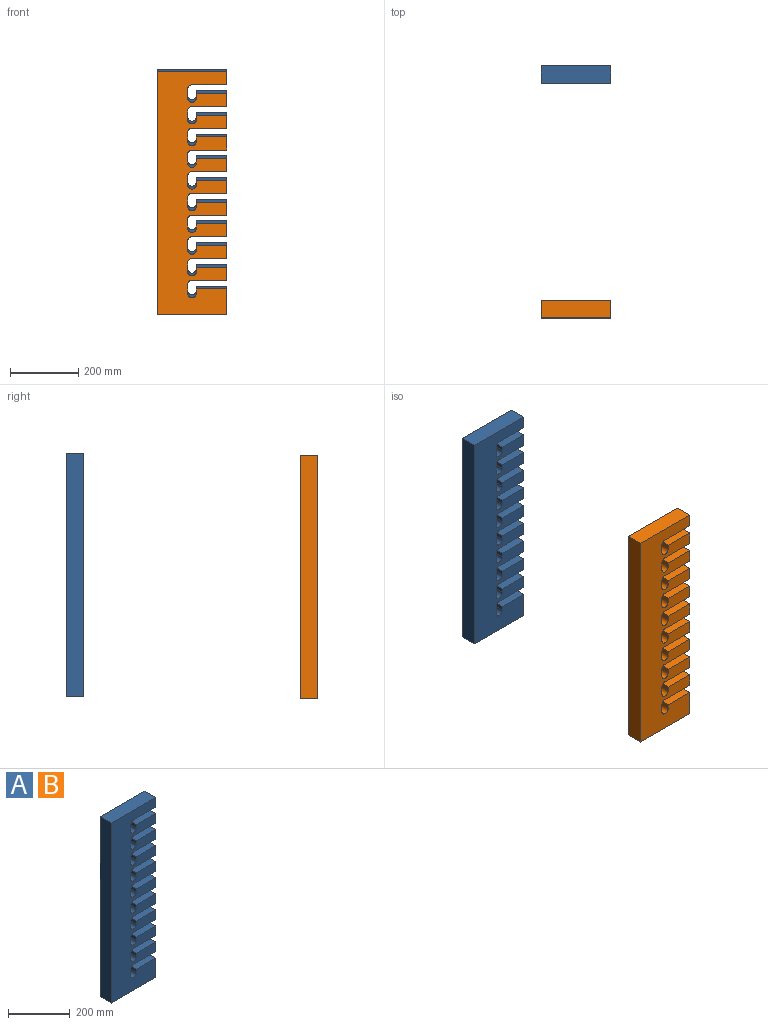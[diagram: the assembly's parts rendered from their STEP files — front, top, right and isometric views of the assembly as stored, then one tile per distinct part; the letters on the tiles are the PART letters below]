
ASSEMBLY  parts=2 mates=2
PART A: 76 faces, bbox 203.2x50.8x711.2 mm
  f0: plane 88.9x50.8mm, normal (0,0,1), area 4516.1mm2, adj f1,f73,f74,f75
  f1: plane 50.8x12.7mm, normal (-1,0,0), area 645.2mm2, adj f0,f2,f74,f75
  f2: cylinder r=12.7mm len=50.8mm, axis (0,1,0), area 2026.8mm2, adj f1,f3,f74,f75
  f3: plane 50.8x25.4mm, normal (1,0,0), area 1290.3mm2, adj f2,f4,f74,f75
  f4: cylinder r=12.7mm len=50.8mm, axis (0,1,0), area 1013.4mm2, adj f3,f5,f74,f75
  f5: plane 101.6x50.8mm, normal (0,0,-1), area 5161.3mm2, adj f4,f6,f74,f75
  f6: plane 50.8x38.1mm, normal (1,0,0), area 1935.5mm2, adj f5,f7,f74,f75
  f7: plane 88.9x50.8mm, normal (0,0,1), area 4516.1mm2, adj f6,f8,f74,f75
  f8: plane 50.8x12.7mm, normal (-1,0,0), area 645.2mm2, adj f7,f9,f74,f75
  f9: cylinder r=12.7mm len=50.8mm, axis (0,1,0), area 2026.8mm2, adj f8,f10,f74,f75
  f10: plane 50.8x25.4mm, normal (1,0,0), area 1290.3mm2, adj f9,f11,f74,f75
  f11: cylinder r=12.7mm len=50.8mm, axis (0,1,0), area 1013.4mm2, adj f10,f12,f74,f75
  f12: plane 101.6x50.8mm, normal (0,0,-1), area 5161.3mm2, adj f11,f13,f74,f75
  f13: plane 50.8x38.1mm, normal (1,0,0), area 1935.5mm2, adj f12,f14,f74,f75
  f14: plane 88.9x50.8mm, normal (0,0,1), area 4516.1mm2, adj f13,f15,f74,f75
  f15: plane 50.8x12.7mm, normal (-1,0,0), area 645.2mm2, adj f14,f16,f74,f75
  f16: cylinder r=12.7mm len=50.8mm, axis (0,1,0), area 2026.8mm2, adj f15,f17,f74,f75
  f17: plane 50.8x25.4mm, normal (1,0,0), area 1290.3mm2, adj f16,f18,f74,f75
  f18: cylinder r=12.7mm len=50.8mm, axis (0,1,0), area 1013.4mm2, adj f17,f19,f74,f75
  f19: plane 101.6x50.8mm, normal (0,0,-1), area 5161.3mm2, adj f18,f20,f74,f75
  f20: plane 50.8x38.1mm, normal (1,0,0), area 1935.5mm2, adj f19,f21,f74,f75
  f21: plane 88.9x50.8mm, normal (0,0,1), area 4516.1mm2, adj f20,f22,f74,f75
  f22: plane 50.8x12.7mm, normal (-1,0,0), area 645.2mm2, adj f21,f23,f74,f75
  f23: cylinder r=12.7mm len=50.8mm, axis (0,1,0), area 2026.8mm2, adj f22,f24,f74,f75
  f24: plane 50.8x25.4mm, normal (1,0,0), area 1290.3mm2, adj f23,f25,f74,f75
  f25: cylinder r=12.7mm len=50.8mm, axis (0,1,0), area 1013.4mm2, adj f24,f26,f74,f75
  f26: plane 101.6x50.8mm, normal (0,0,-1), area 5161.3mm2, adj f25,f27,f74,f75
  f27: plane 50.8x38.1mm, normal (1,0,0), area 1935.5mm2, adj f26,f28,f74,f75
  f28: plane 88.9x50.8mm, normal (0,0,1), area 4516.1mm2, adj f27,f29,f74,f75
  f29: plane 50.8x12.7mm, normal (-1,0,0), area 645.2mm2, adj f28,f30,f74,f75
  f30: cylinder r=12.7mm len=50.8mm, axis (0,1,0), area 2026.8mm2, adj f29,f31,f74,f75
  f31: plane 50.8x25.4mm, normal (1,0,0), area 1290.3mm2, adj f30,f32,f74,f75
  f32: cylinder r=12.7mm len=50.8mm, axis (0,1,0), area 1013.4mm2, adj f31,f33,f74,f75
  f33: plane 101.6x50.8mm, normal (0,0,-1), area 5161.3mm2, adj f32,f34,f74,f75
  f34: plane 50.8x38.1mm, normal (1,0,0), area 1935.5mm2, adj f33,f35,f74,f75
  f35: plane 88.9x50.8mm, normal (0,0,1), area 4516.1mm2, adj f34,f36,f74,f75
  f36: plane 50.8x12.7mm, normal (-1,0,0), area 645.2mm2, adj f35,f37,f74,f75
  f37: cylinder r=12.7mm len=50.8mm, axis (0,1,0), area 2026.8mm2, adj f36,f38,f74,f75
  f38: plane 50.8x25.4mm, normal (1,0,0), area 1290.3mm2, adj f37,f39,f74,f75
  f39: cylinder r=12.7mm len=50.8mm, axis (0,1,0), area 1013.4mm2, adj f38,f40,f74,f75
  f40: plane 101.6x50.8mm, normal (0,0,-1), area 5161.3mm2, adj f39,f41,f74,f75
  f41: plane 50.8x38.1mm, normal (1,0,0), area 1935.5mm2, adj f40,f42,f74,f75
  f42: plane 88.9x50.8mm, normal (0,0,1), area 4516.1mm2, adj f41,f43,f74,f75
  f43: plane 50.8x12.7mm, normal (-1,0,0), area 645.2mm2, adj f42,f44,f74,f75
  f44: cylinder r=12.7mm len=50.8mm, axis (0,1,0), area 2026.8mm2, adj f43,f45,f74,f75
  f45: plane 50.8x25.4mm, normal (1,0,0), area 1290.3mm2, adj f44,f46,f74,f75
  f46: cylinder r=12.7mm len=50.8mm, axis (0,1,0), area 1013.4mm2, adj f45,f47,f74,f75
  f47: plane 101.6x50.8mm, normal (0,0,-1), area 5161.3mm2, adj f46,f48,f74,f75
  f48: plane 50.8x38.1mm, normal (1,0,0), area 1935.5mm2, adj f47,f49,f74,f75
  f49: plane 88.9x50.8mm, normal (0,0,1), area 4516.1mm2, adj f48,f50,f74,f75
  f50: plane 50.8x12.7mm, normal (-1,0,0), area 645.2mm2, adj f49,f51,f74,f75
  f51: cylinder r=12.7mm len=50.8mm, axis (0,1,0), area 2026.8mm2, adj f50,f52,f74,f75
  f52: plane 50.8x25.4mm, normal (1,0,0), area 1290.3mm2, adj f51,f53,f74,f75
  f53: cylinder r=12.7mm len=50.8mm, axis (0,1,0), area 1013.4mm2, adj f52,f54,f74,f75
  f54: plane 101.6x50.8mm, normal (0,0,-1), area 5161.3mm2, adj f53,f55,f74,f75
  f55: plane 50.8x38.1mm, normal (1,0,0), area 1935.5mm2, adj f54,f56,f74,f75
  f56: plane 88.9x50.8mm, normal (0,0,1), area 4516.1mm2, adj f55,f57,f74,f75
  f57: plane 50.8x12.7mm, normal (-1,0,0), area 645.2mm2, adj f56,f58,f74,f75
  f58: cylinder r=12.7mm len=50.8mm, axis (0,1,0), area 2026.8mm2, adj f57,f59,f74,f75
  f59: plane 50.8x25.4mm, normal (1,0,0), area 1290.3mm2, adj f58,f60,f74,f75
  f60: cylinder r=12.7mm len=50.8mm, axis (0,1,0), area 1013.4mm2, adj f59,f61,f74,f75
  f61: plane 101.6x50.8mm, normal (0,0,-1), area 5161.3mm2, adj f60,f62,f74,f75
  f62: plane 50.8x38.1mm, normal (1,0,0), area 1935.5mm2, adj f61,f63,f74,f75
  f63: plane 88.9x50.8mm, normal (0,0,1), area 4516.1mm2, adj f62,f64,f74,f75
  f64: plane 50.8x12.7mm, normal (-1,0,0), area 645.2mm2, adj f63,f65,f74,f75
  f65: cylinder r=12.7mm len=50.8mm, axis (0,1,0), area 2026.8mm2, adj f64,f66,f74,f75
  f66: plane 50.8x25.4mm, normal (1,0,0), area 1290.3mm2, adj f65,f67,f74,f75
  f67: cylinder r=12.7mm len=50.8mm, axis (0,1,0), area 1013.4mm2, adj f66,f68,f74,f75
  f68: plane 101.6x50.8mm, normal (0,0,-1), area 5161.3mm2, adj f67,f69,f74,f75
  f69: plane 50.8x38.1mm, normal (1,0,0), area 1935.5mm2, adj f68,f70,f74,f75
  f70: plane 203.2x50.8mm, normal (0,0,1), area 10322.6mm2, adj f69,f71,f74,f75
  f71: plane 711.2x50.8mm, normal (-1,0,0), area 36129mm2, adj f70,f72,f74,f75
  f72: plane 203.2x50.8mm, normal (0,0,-1), area 10322.6mm2, adj f71,f73,f74,f75
  f73: plane 76.2x50.8mm, normal (1,0,0), area 3871mm2, adj f0,f72,f74,f75
  f74: plane 711.2x203.2mm, normal (0,-1,0), area 110070.4mm2, adj f0,f1,f2,f3,f4,f5,f6,f7
  f75: plane 711.2x203.2mm, normal (0,1,0), area 110070.4mm2, adj f0,f1,f2,f3,f4,f5,f6,f7
PART B: same geometry as A
PLACE A t=(106.57,-381.87,-31.44)mm
PLACE B t=(106.57,-1067.74,-39.74)mm
MATE planar A.f71 <-> B.f71  axis (-1,0,0) through (4.97,-407.27,-31.44)mm
MATE parallel A.f71 <-> B.f71  axis (-1,0,0) through (4.97,-407.27,-31.44)mm
